# Revit family: 0053322 Feilo Sylvania Lighting Fixture SYLFLAT SURFACE DIM 1600 R 4000K
name_source: partatom
category: Lighting Fixtures
revit_build: Autodesk Revit 2016 (Build: 20150220_1215(x64)
units: mm (PartAtom-declared; Revit-internal decimal feet)

## family parameters
Cut with Voids When Loaded = No
Host = Face
Light Source = Yes
OmniClass Number = 23.80.70.00
OmniClass Title = Lighting
Part Type = Normal
Room Calculation Point = No
Round Connector Dimension = Use Diameter
Shared = No

## types (1)
- 0053322 SYLFLAT SURFACE DIM 1600 R 4000K
    Apparent Load = 18 VA
    Assembly Code = D5020200
    AssetType = Fixed
    ClassificationName = Uniclass2015
    ClassificationValue = EF_70_80
    Color Filter = 16777215
    Cost = 0 $
    Default Elevation = 1219 mm
    Description = Integrated LED surface mounted downlight providing 1790 fixture lumens at a wattage of 18W giving a high efficacy of 99lm/W. Fitting includes Leading/Trailing edge phase dimmable driver and has a round outer dimmension of of 226x226x39mm with an IP20 and IK02 rating providing uniform distribution with an Opal diffuser and 110° beam angle. Provided including a Loop in Loop out box and built with a white aluminium housing.
    Dimming Lamp Color Temperature Shift = <None>
    DimmingControlOptions = Dimmable
    DocumentationLiterature = http://www.feilosylvania.com
    DurationUnit = hours
    ElectricShockClassification = Class II
    Emit Shape Visible in Rendering = No
    Emit from Circle Diameter = 170 mm
    ExpectedLife = 50000
    IfcExportAs = IfcLightFixtureType
    IfcExportType = IfcLightFixtureType
    ImpactProtectionIndex = IK06
    IngressProtection = IP20
    InputNominalFrequency = 50/60 Hz
    InputVoltage = 220-240V~
    Keynote = 16500
    Lamp = LED
    LampColourRenderingIndex = 80
    LampColourTemperature = 4000 K
    LampNominalLuminous = 1600 lm
    LampsType = LED
    LuminousEfficacy = 99.44 lm/W
    Manufacturer = Feilo Sylvania
    ManufacturerName = Feilo Sylvania
    Material = aluminium housing, polystyrene diffuser
    Material_1_FEILO = Body-Sylvania-SylflatSurface-White
    Material_2_FEILO = LED-Sylvania-SylflatSurface
    Material_3_FEILO = <By Category>
    Material_4_FEILO = <By Category>
    Model = SYLFLAT SURFACE DIM 1600 R 4000K
    ModelNumber = 0053322
    ModelReference = SYLFLAT SURFACE DIM 1600 R 4000K
    Name = SYLFLAT SURFACE DIM 1600 R 4000K
    NominalDepth = 226 mm  [stored 0.74147 ft]
    NominalHeight = 39 mm  [stored 0.127953 ft]
    NominalLength = 226 mm  [stored 0.74147 ft]
    Photometric Web File = 0053322.ies
    PowerConsumption = 18 W
    PowerFactor = 0.9
    RadiusDiffuser_FEILO = 7 mm  [stored 0.0229659 ft]
    RadiusSquare_FEILO = 10 mm  [stored 0.0328084 ft]
    Round_FEILO = Yes
    Square_FEILO = No
    Tilt Angle = -90.00°
    Type Image = <None>
    TypeName = SYLFLAT SURFACE DIM 1600 R 4000K
    URL = http://www.feilosylvania.com
    Voltage = 230 V
    Weight = 6.59 kg
    WidthDiffuser_FEILO = 170 mm
    Width_FEILO = 226 mm  [stored 0.74147 ft]

note: [stored X ft] marks values corroborated as IEEE doubles in the binary element streams (Revit-internal decimal feet)

## geometry (parser evidence)
native form markers: Sweep x2
no freeform markers — native parametric forms only
